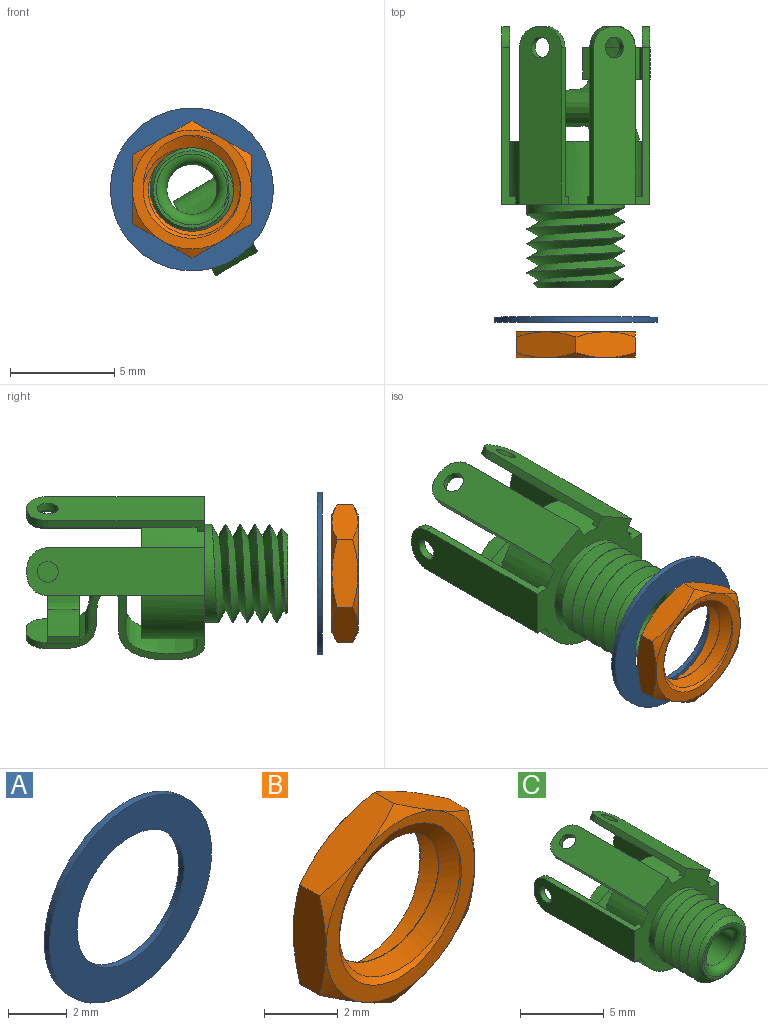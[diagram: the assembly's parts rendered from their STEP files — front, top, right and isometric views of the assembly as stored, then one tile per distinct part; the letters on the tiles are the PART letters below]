
ASSEMBLY  parts=3 mates=2
PART A: 4 faces, bbox 7.8x0.3x7.8 mm
  f0: cylinder r=2.58mm len=5.16mm, axis (0,1,0), area 4.1mm2, adj f2,f3
  f1: cylinder r=3.9mm len=7.8mm, axis (0,1,0), area 6.1mm2, adj f2,f3
  f2: plane 7.8x7.8mm, normal (0,-1,0), area 26.9mm2, adj f0,f1
  f3: plane 7.8x7.8mm, normal (0,1,0), area 26.9mm2, adj f0,f1
PART B: 24 faces, bbox 7.1x2.6x7.1 mm
  f0: cylinder r=2mm len=4mm, axis (0,1,0), area 0.2mm2, adj f1,f21,f22,f23
  f1: plane 6.17x6.17mm, normal (0,1,0), area 8.9mm2, adj f0,f5,f6,f8,f10,f12,f14,f22
  f2: plane 5.81x5.81mm, normal (0,-1,0), area 7.5mm2, adj f3,f4,f7,f9,f11,f13,f21,f22
  f3: cone r=3.93mm half-angle=60deg, axis (0,1,0), area 0.8mm2, adj f2,f15,f16
  f4: cone r=3.93mm half-angle=60deg, axis (0,1,0), area 0.8mm2, adj f2,f15,f20
  f5: cone r=3.93mm half-angle=60deg, axis (0,-1,0), area 0.8mm2, adj f1,f15,f16
  f6: cone r=3.93mm half-angle=60deg, axis (0,-1,0), area 0.8mm2, adj f1,f15,f20
  f7: cone r=3.93mm half-angle=60deg, axis (0,1,0), area 0.8mm2, adj f2,f16,f17
  f8: cone r=3.93mm half-angle=60deg, axis (0,-1,0), area 0.8mm2, adj f1,f16,f17
  f9: cone r=3.93mm half-angle=60deg, axis (0,1,0), area 0.8mm2, adj f2,f17,f18
  f10: cone r=3.93mm half-angle=60deg, axis (0,-1,0), area 0.8mm2, adj f1,f17,f18
  f11: cone r=3.93mm half-angle=60deg, axis (0,1,0), area 0.8mm2, adj f2,f18,f19
  f12: cone r=3.93mm half-angle=60deg, axis (0,-1,0), area 0.8mm2, adj f1,f18,f19
  f13: cone r=3.93mm half-angle=60deg, axis (0,1,0), area 0.8mm2, adj f2,f19,f20
  f14: cone r=3.93mm half-angle=60deg, axis (0,-1,0), area 0.8mm2, adj f1,f19,f20
  f15: plane 3.57x1.53mm, normal (1,0,0), area 3.5mm2, adj f3,f4,f5,f6,f16,f20
  f16: plane 3.13x1.92mm, normal (0.5,0,-0.87), area 3.5mm2, adj f3,f5,f7,f8,f15,f17
  f17: plane 3.13x1.92mm, normal (-0.5,0,-0.87), area 3.5mm2, adj f7,f8,f9,f10,f16,f18
  f18: plane 3.57x1.53mm, normal (-1,0,0), area 3.5mm2, adj f9,f10,f11,f12,f17,f19
  f19: plane 3.13x1.92mm, normal (-0.5,0,0.87), area 3.5mm2, adj f11,f12,f13,f14,f18,f20
  f20: plane 3.13x1.92mm, normal (0.5,0,0.87), area 3.5mm2, adj f4,f6,f13,f14,f15,f19
  f21: cone r=2mm half-angle=45deg, axis (0,-1,0), area 2mm2, adj f0,f2,f22,f23
  f22: bspline ~5.99x5.19mm, area 16.6mm2, adj f0,f1,f2,f21,f23
  f23: bspline ~5.99x5.19mm, area 16.4mm2, adj f0,f1,f2,f21,f22
PART C: 60 faces, bbox 8.1x14x8.8 mm
  f0: plane 6x0.61mm, normal (0,0,-1), area 2.3mm2, adj f1,f3,f4,f14,f27,f55
  f1: plane 8.5x2.3mm, normal (1,0,0), area 19.1mm2, adj f0,f3,f13,f28,f44,f45,f56
  f2: extruded ~5.67x4.41mm, area 25.5mm2, adj f21,f22,f23,f55
  f3: plane 7.09x6.97mm, normal (0,-1,0), area 18.2mm2, adj f0,f1,f4,f6,f10,f11,f13,f15
  f4: cylinder r=3.12mm len=6.25mm, axis (0,1,0), area 54.8mm2, adj f0,f3,f8,f10,f11,f12,f13,f14
  f5: cylinder r=1.2mm len=6.5mm, axis (0,1,0), area 49mm2, adj f8,f9
  f6: cylinder r=2.35mm len=4.7mm, axis (0,1,0), area 6.4mm2, adj f3,f51,f52,f53,f54
  f7: plane 3.73x3.66mm, normal (0,-1,0), area 1.6mm2, adj f9,f51,f53,f54
  f8: plane 6.25x6.25mm, normal (0,1,0), area 26.2mm2, adj f4,f5
  f9: torus R=1.7mm, axis (0,-1,0), area 6.8mm2, adj f5,f7
  f10: plane 7.5x0.67mm, normal (0,0,1), area 2.9mm2, adj f3,f4,f12,f24,f25,f46
  f11: plane 7.5x0.61mm, normal (0,0,-1), area 2.9mm2, adj f3,f4,f12,f24,f25,f47
  f12: plane 2.3x0.3mm, normal (0,1,0), area 0.3mm2, adj f4,f10,f11,f24
  f13: plane 7.5x0.67mm, normal (0,0,1), area 2.9mm2, adj f1,f3,f4,f14,f27,f45
  f14: plane 2.3x0.3mm, normal (0,1,0), area 0.3mm2, adj f0,f4,f13,f27
  f15: plane 7.5x0.58mm, normal (0.87,0,0.5), area 2.9mm2, adj f3,f4,f17,f29,f30,f43
  f16: plane 7.5x0.53mm, normal (-0.87,0,-0.5), area 2.9mm2, adj f3,f4,f17,f29,f30,f42
  f17: plane 2.14x1.36mm, normal (0,1,0), area 0.3mm2, adj f4,f15,f16,f29
  f18: plane 7.5x0.58mm, normal (0.87,0,-0.5), area 2.9mm2, adj f3,f4,f20,f32,f33,f41
  f19: plane 7.5x0.53mm, normal (-0.87,0,0.5), area 2.9mm2, adj f3,f4,f20,f32,f33,f40
  f20: plane 2.11x1.41mm, normal (0,1,0), area 0.3mm2, adj f4,f18,f19,f32
  f21: plane 7.57x3.69mm, normal (0.87,0,0.5), area 4.5mm2, adj f2,f3,f4,f23,f35,f37,f39,f55
  f22: plane 8.53x4.54mm, normal (-0.87,0,-0.5), area 4.5mm2, adj f2,f3,f4,f23,f35,f37,f38,f55
  f23: plane 2.11x1.41mm, normal (0,1,0), area 0.3mm2, adj f2,f4,f21,f22
  f24: plane 8.15x2.3mm, normal (1,0,0), area 17.5mm2, adj f10,f11,f12,f26,f46,f47,f50
  f25: plane 8.5x2.3mm, normal (-1,0,0), area 18.3mm2, adj f3,f10,f11,f26,f46,f47,f50
  f26: plane 0.37x0.3mm, normal (0,1,0), area 0.1mm2, adj f24,f25,f46,f47
  f27: plane 8.15x2.3mm, normal (-1,0,0), area 18.3mm2, adj f0,f13,f14,f28,f44,f45,f58
  f28: plane 0.37x0.3mm, normal (0,1,0), area 0.1mm2, adj f1,f27,f44,f45
  f29: plane 8.15x1.99mm, normal (0.5,0,-0.87), area 17.5mm2, adj f15,f16,f17,f31,f42,f43,f48
  f30: plane 8.5x1.99mm, normal (-0.5,0,0.87), area 18.3mm2, adj f3,f15,f16,f31,f42,f43,f48
  f31: plane 0.47x0.45mm, normal (0,1,0), area 0.1mm2, adj f29,f30,f42,f43
  f32: plane 8.15x1.99mm, normal (-0.5,0,-0.87), area 17.5mm2, adj f18,f19,f20,f34,f40,f41,f49
  f33: plane 8.5x1.99mm, normal (0.5,0,0.87), area 18.3mm2, adj f3,f18,f19,f34,f40,f41,f49
  f34: plane 0.47x0.45mm, normal (0,1,0), area 0.1mm2, adj f32,f33,f40,f41
  f35: extruded ~8.54x4.42mm, area 32.1mm2, adj f3,f21,f22,f36,f38,f39
  f36: plane 0.45x0.43mm, normal (-0.01,1,0.01), area 0.1mm2, adj f35,f37,f38,f39
  f37: extruded ~2.23x2.03mm, area 4.5mm2, adj f21,f22,f36,f38,f39,f56
  f38: cylinder r=1mm len=1.05mm, axis (-0.5,-0.01,0.87), area 0.5mm2, adj f22,f35,f36,f37
  f39: cylinder r=1mm len=1.06mm, axis (-0.5,-0.01,0.87), area 0.5mm2, adj f21,f35,f36,f37
  f40: cylinder r=1mm len=1.05mm, axis (0.5,0,0.87), area 0.6mm2, adj f19,f32,f33,f34
  f41: cylinder r=1mm len=1.05mm, axis (-0.5,0,-0.87), area 0.6mm2, adj f18,f32,f33,f34
  f42: cylinder r=1mm len=1.05mm, axis (-0.5,0,0.87), area 0.6mm2, adj f16,f29,f30,f31
  f43: cylinder r=1mm len=1.05mm, axis (0.5,0,-0.87), area 0.6mm2, adj f15,f29,f30,f31
  f44: cylinder r=1mm len=1mm, axis (-1,0,0), area 0.6mm2, adj f1,f27,f28,f59
  f45: cylinder r=1mm len=1mm, axis (1,0,0), area 0.6mm2, adj f1,f13,f27,f28
  f46: cylinder r=1mm len=1mm, axis (1,0,0), area 0.6mm2, adj f10,f24,f25,f26
  f47: cylinder r=1mm len=1mm, axis (-1,0,0), area 0.6mm2, adj f11,f24,f25,f26
  f48: cylinder r=0.5mm len=1.05mm, axis (-0.5,0,0.87), area 1.2mm2, adj f29,f30
  f49: cylinder r=0.5mm len=1.05mm, axis (0.5,0,0.87), area 1.2mm2, adj f32,f33
  f50: cylinder r=0.5mm len=1mm, axis (-1,0,0), area 1.2mm2, adj f24,f25
  f51: cone r=1.85mm half-angle=45deg, axis (0,1,0), area 3.9mm2, adj f6,f7,f53,f54
  f52: plane 0.69x0.58mm, normal (0.97,0,0.22), area 0.2mm2, adj f6,f53,f54
  f53: bspline ~5.43x4.7mm, area 41.1mm2, adj f6,f7,f51,f52,f54
  f54: bspline ~5.43x4.7mm, area 45.7mm2, adj f6,f7,f51,f52,f53
  f55: plane 3.22x2.28mm, normal (0,-1,0), area 1.2mm2, adj f0,f2,f21,f22,f56,f57,f58
  f56: extruded ~3.04x2.28mm, area 5.3mm2, adj f1,f21,f22,f37,f55,f57,f59
  f57: plane 1.5x0.32mm, normal (-0.87,0,-0.49), area 0.6mm2, adj f55,f56,f58,f59
  f58: extruded ~2.85x1.95mm, area 5.6mm2, adj f27,f55,f57,f59
  f59: plane 3.22x2.29mm, normal (0,1,0), area 1.5mm2, adj f44,f56,f57,f58
PLACE A t=(16.93,-6.83,1.18)mm
PLACE B t=(16.93,-7.29,1.18)mm
PLACE C t=(16.93,-5.42,1.18)mm
MATE slider B.f0 <-> C.f4  axis (0,-1,0) through (16.93,-14.54,1.18)mm
MATE slider A.f0 <-> C.f4  axis (0,-1,0) through (16.93,-13.96,1.18)mm
